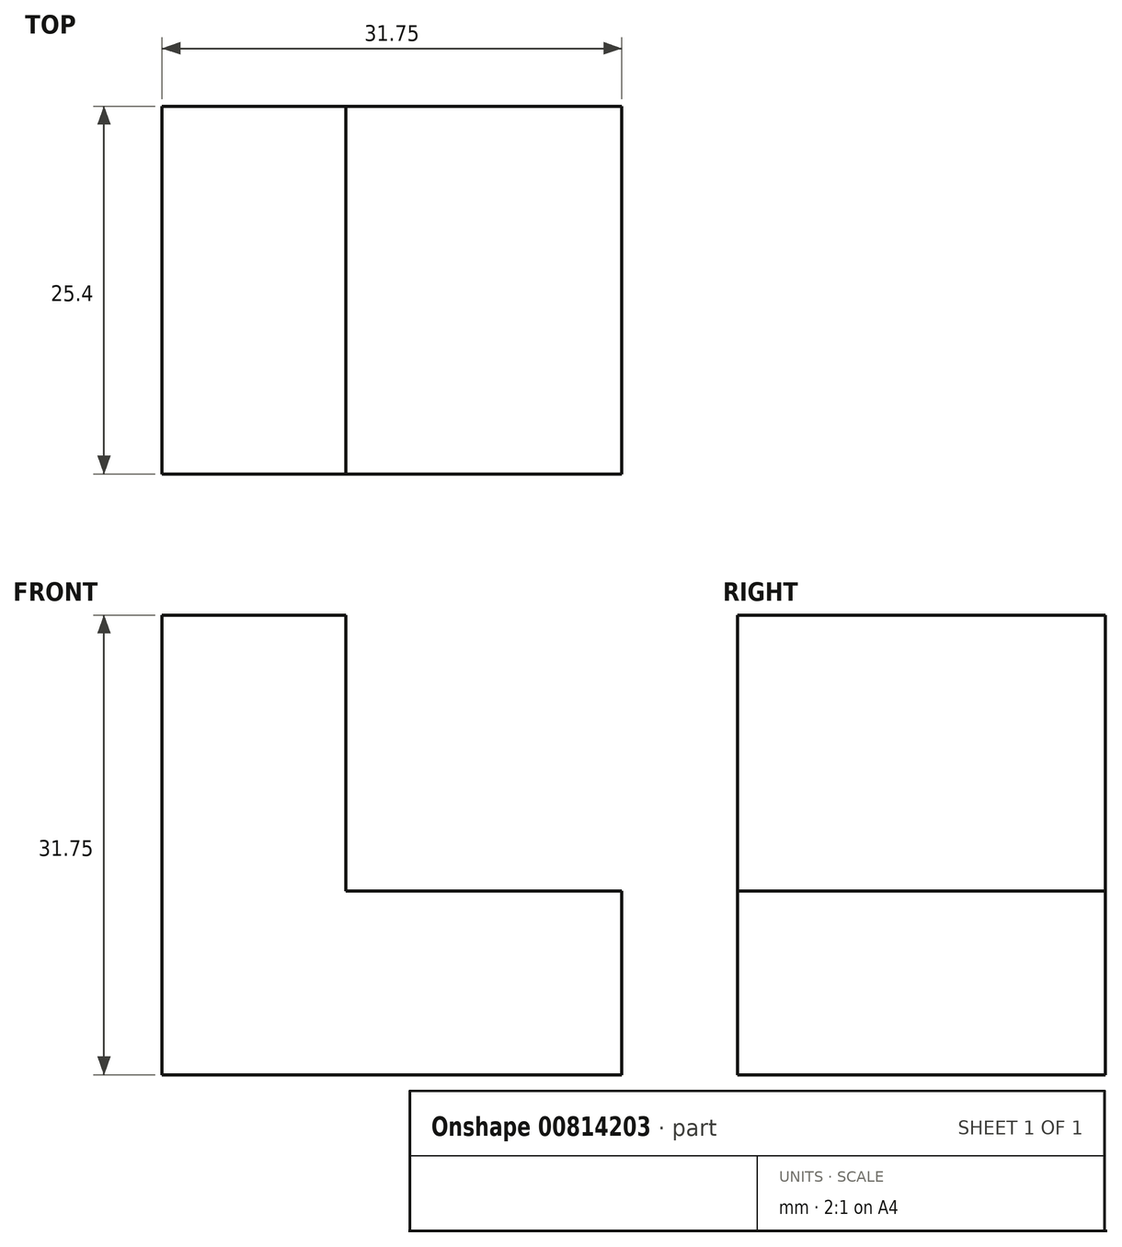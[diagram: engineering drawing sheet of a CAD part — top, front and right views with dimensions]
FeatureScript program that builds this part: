
annotation { "Feature Type Name" : "Feature", "Feature Type Description" : "" }
export const myFeature = defineFeature(function(context is Context, id is Id, definition is map)
    precondition{}
    {
        {
            var Q0;
            Q0=qCreatedBy(makeId("Front.planeOp"),FACE);
            var sketch = newSketch(context, id + "F0", { "sketchPlane" : qUnion([Q0])});
            skLineSegment(sketch, "E0", {"start": v(0, 0) * mm, "end": v(0, 31.75) * mm});
            skLineSegment(sketch, "E1", {"start": v(0, 31.75) * mm, "end": v(12.7, 31.75) * mm});
            skLineSegment(sketch, "E2", {"start": v(12.7, 31.75) * mm, "end": v(12.7, 12.7) * mm});
            skLineSegment(sketch, "E3", {"start": v(12.7, 12.7) * mm, "end": v(31.75, 12.7) * mm});
            skLineSegment(sketch, "E4", {"start": v(31.75, 12.7) * mm, "end": v(31.75, 0) * mm});
            skLineSegment(sketch, "E5", {"start": v(0, 0) * mm, "end": v(31.75, 0) * mm});
            skSolve(sketch);
        }
        {
            var Q0;
            Q0=makeQuery(id+"F0.imprint","IMPRINT",FACE,{"disambiguationData":[TD([[makeQuery(id+"F0.imprint","IMPRINT",EDGE,{"derivedFrom":sQuery(id+"F0.wireOp",EDGE,"E0")}),-1.0]])]});
            extrude(context, id + "F1", {"entities" : qUnion([Q0]), "depth" : 25.4 * mm, "offsetDistance" : 25.4 * mm});
        }
    });
